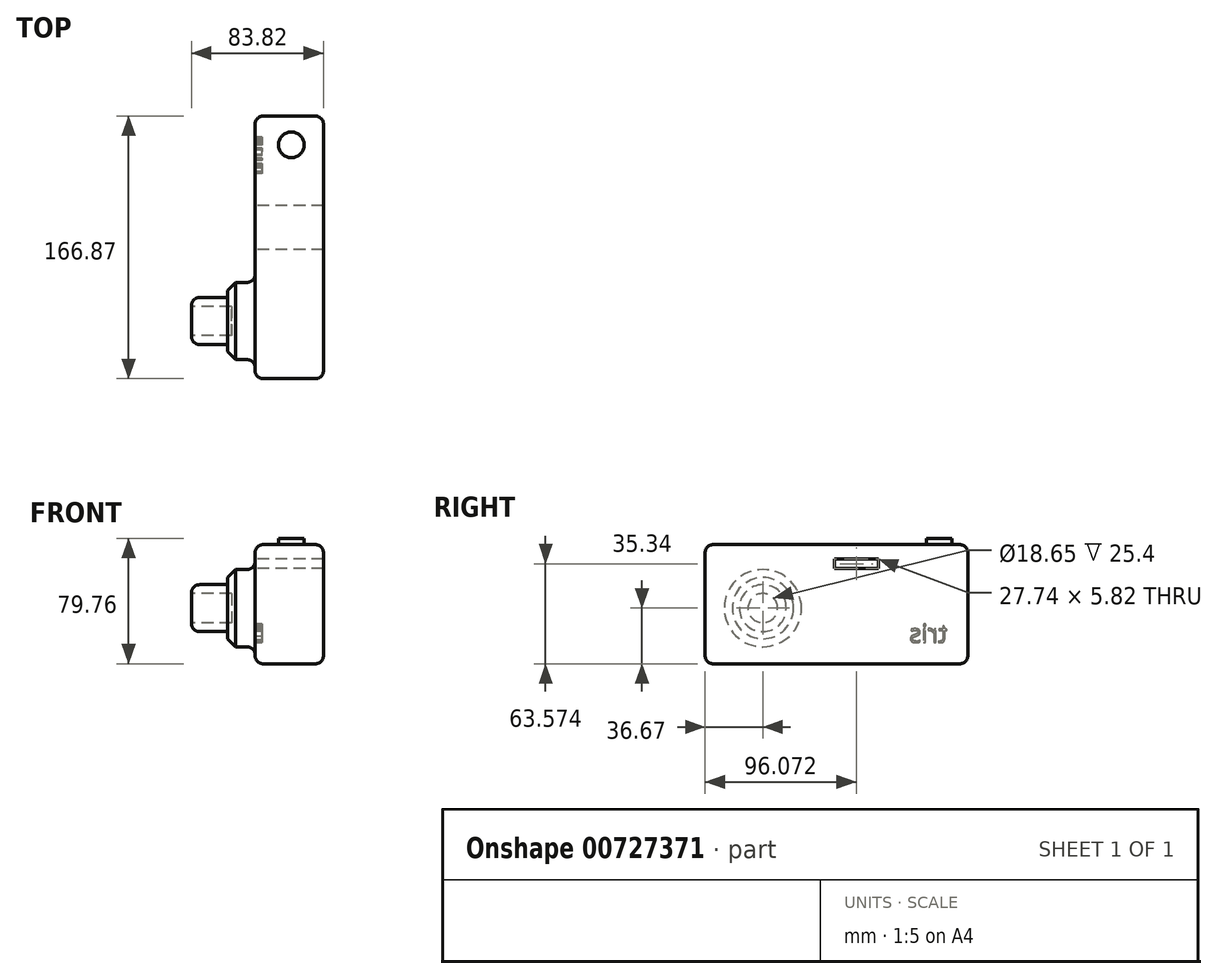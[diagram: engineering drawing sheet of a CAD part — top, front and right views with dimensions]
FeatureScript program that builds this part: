
annotation { "Feature Type Name" : "Feature", "Feature Type Description" : "" }
export const myFeature = defineFeature(function(context is Context, id is Id, definition is map)
    precondition{}
    {
        {
            var Q0;
            Q0=qCreatedBy(makeId("Top.planeOp"),FACE);
            var sketch = newSketch(context, id + "F0", { "sketchPlane" : qUnion([Q0])});
            skLineSegment(sketch, "E0.bottom", {"start": v(-47.57, -71.21) * mm, "end": v(-91, -71.21) * mm});
            skLineSegment(sketch, "E0.top", {"start": v(-47.57, 95.66) * mm, "end": v(-91, 95.66) * mm});
            skLineSegment(sketch, "E0.left", {"start": v(-47.57, -71.21) * mm, "end": v(-47.57, 95.66) * mm});
            skLineSegment(sketch, "E0.right", {"start": v(-91, -71.21) * mm, "end": v(-91, 95.66) * mm});
            skSolve(sketch);
        }
        {
            var Q0;
            Q0 = qSketchRegion(id + "F0", true);
            extrude(context, id + "F1", {"entities" : qUnion([Q0]), "depth" : 75.7 * mm, "offsetDistance" : 25.4 * mm});
        }
        {
            var Q0;
            Q0=makeQuery(id+"F1.opExtrude","SWEPT_FACE",FACE,{"disambiguationData":[OSD([sQuery(id+"F0.wireOp",EDGE,"E0.right")])]});
            var sketch = newSketch(context, id + "F2", { "sketchPlane" : qUnion([Q0])});
            skCircle(sketch, "E1", {"center": v(34.54, 35.34) * mm, "radius": 24.52 * mm});
            skSolve(sketch);
        }
        {
            var Q0;
            Q0 = qSketchRegion(id + "F2", true);
            extrude(context, id + "F3", {"entities" : qUnion([Q0]), "operationType" : NewBodyOperationType.ADD, "depth" : 17.53 * mm, "offsetDistance" : 25.4 * mm});
        }
        {
            var Q0;
            Q0=makeQuery(id+"F3.opExtrude","CAP_FACE",FACE,{"disambiguationData":[OSD([sQuery(id+"F2.wireOp",EDGE,"E1")])],"isStart":false});
            var sketch = newSketch(context, id + "F4", { "sketchPlane" : qUnion([Q0])});
            skCircle(sketch, "E2", {"center": v(34.54, 35.34) * mm, "radius": 14.9 * mm});
            skSolve(sketch);
        }
        {
            var Q0;
            Q0=makeQuery(id+"F4.imprint","IMPRINT",FACE,{"disambiguationData":[TD([[makeQuery(id+"F4.imprint","IMPRINT",EDGE,{"derivedFrom":sQuery(id+"F4.wireOp",EDGE,"E2")}),1.0]])]});
            var sketch = newSketch(context, id + "F5", { "sketchPlane" : qUnion([Q0])});
            skSolve(sketch);
        }
        {
            var Q0;
            Q0 = qSketchRegion(id + "F5", true);
            var Q1;
            Q1=makeQuery(id+"F5.imprint","IMPRINT",FACE,{"disambiguationData":[TD([[makeQuery(id+"F5.imprint","IMPRINT",EDGE,{"derivedFrom":makeQuery(id+"F4.imprint","IMPRINT",EDGE,{"derivedFrom":sQuery(id+"F4.wireOp",EDGE,"E2")})}),1.0]])]});
            extrude(context, id + "F6", {"entities" : qUnion([Q0, Q1]), "operationType" : NewBodyOperationType.ADD, "depth" : 5.33 * mm, "offsetDistance" : 25.4 * mm});
        }
        {
            var Q0;
            Q0=makeQuery(id+"F1.opExtrude","SWEPT_FACE",FACE,{"disambiguationData":[OSD([sQuery(id+"F0.wireOp",EDGE,"E0.right")])]});
            fillet(context, id + "F7", {"entities" : qUnion([Q0]), "radius" : 5.08 * mm, "tangentPropagation" : true, "allowEdgeOverflow" : false});
        }
        {
            var Q0;
            Q0=makeQuery(id+"F1.opExtrude","SWEPT_FACE",FACE,{"disambiguationData":[OSD([sQuery(id+"F0.wireOp",EDGE,"E0.bottom")])]});
            fillet(context, id + "F8", {"entities" : qUnion([Q0]), "radius" : 5.08 * mm, "tangentPropagation" : true, "allowEdgeOverflow" : false});
        }
        {
            var Q0;
            Q0=makeQuery(id+"F1.opExtrude","SWEPT_FACE",FACE,{"disambiguationData":[OSD([sQuery(id+"F0.wireOp",EDGE,"E0.left")])]});
            fillet(context, id + "F9", {"entities" : qUnion([Q0]), "radius" : 5.08 * mm, "tangentPropagation" : true, "allowEdgeOverflow" : false});
        }
        {
            var Q0;
            Q0=makeQuery(id+"F1.opExtrude","SWEPT_FACE",FACE,{"disambiguationData":[OSD([sQuery(id+"F0.wireOp",EDGE,"E0.top")])]});
            fillet(context, id + "F10", {"entities" : qUnion([Q0]), "radius" : 5.08 * mm, "tangentPropagation" : true, "allowEdgeOverflow" : false});
        }
        {
            var Q0;
            Q0=makeQuery(id+"F1.opExtrude","SWEPT_FACE",FACE,{"disambiguationData":[OSD([sQuery(id+"F0.wireOp",EDGE,"E0.right")])]});
            var sketch = newSketch(context, id + "F11", { "sketchPlane" : qUnion([Q0])});
            skText(sketch, "E3", { "text": "tris", "fontName": "OpenSans-Regular.ttf"});
            const initialGuessF11  = {"E3": [-0.08247, 0.01358, 1, 0, 0.01158]};
            skSetInitialGuess(sketch, initialGuessF11);
            skSolve(sketch);
        }
        {
            var Q0;
            Q0 = qSketchRegion(id + "F11", true);
            extrude(context, id + "F12", {"entities" : qUnion([Q0]), "operationType" : NewBodyOperationType.REMOVE, "oppositeDirection" : true, "depth" : 4.6 * mm, "offsetDistance" : 25.4 * mm});
        }
        {
            var Q1;
            Q1=sQuery(id+"F4.wireOp",VERTEX,"E2.center");
            var Q2;
            Q2=makeQuery(id+"F6.opExtrude","CAP_FACE",FACE,{"disambiguationData":[OSD([sQuery(id+"F4.wireOp",EDGE,"E2")])],"isStart":false});
            loft(context, id + "F13", {"operationType" : NewBodyOperationType.ADD, "sheetProfilesArray" : [{ "sheetProfileEntities" : qUnion([Q1]) }, { "sheetProfileEntities" : qUnion([Q2]) }]});
        }
        {
            var Q0;
            Q0=makeQuery(id+"F6.opExtrude","CAP_FACE",FACE,{"disambiguationData":[OSD([sQuery(id+"F4.wireOp",EDGE,"E2")])],"isStart":false});
            extrude(context, id + "F14", {"entities" : qUnion([Q0]), "operationType" : NewBodyOperationType.ADD, "depth" : 17.53 * mm, "offsetDistance" : 25.4 * mm});
        }
        {
            var Q0;
            Q0=makeQuery(id+"F14.opExtrude","CAP_FACE",FACE,{"disambiguationData":[OSD([sQuery(id+"F4.wireOp",EDGE,"E2")])],"isStart":false});
            extrude(context, id + "F15", {"entities" : qUnion([Q0]), "operationType" : NewBodyOperationType.ADD, "oppositeDirection" : true, "depth" : 64 * mm, "offsetDistance" : 25.4 * mm});
        }
        {
            var Q0;
            Q0=makeQuery(id+"F14.opExtrude","CAP_FACE",FACE,{"disambiguationData":[OSD([sQuery(id+"F4.wireOp",EDGE,"E2")])],"isStart":false});
            extrude(context, id + "F16", {"entities" : qUnion([Q0]), "operationType" : NewBodyOperationType.ADD, "oppositeDirection" : true, "depth" : 13.2 * mm, "offsetDistance" : 25.4 * mm});
        }
        {
            var Q0;
            Q0=makeQuery(id+"F14.opExtrude","CAP_FACE",FACE,{"disambiguationData":[OSD([sQuery(id+"F4.wireOp",EDGE,"E2")])],"isStart":false});
            extrude(context, id + "F17", {"entities" : qUnion([Q0]), "operationType" : NewBodyOperationType.ADD, "oppositeDirection" : true, "depth" : 25.4 * mm, "offsetDistance" : 25.4 * mm});
        }
        {
            var Q0;
            Q0=makeQuery(id+"F14.opExtrude","CAP_FACE",FACE,{"disambiguationData":[OSD([sQuery(id+"F4.wireOp",EDGE,"E2")])],"isStart":false});
            var sketch = newSketch(context, id + "F18", { "sketchPlane" : qUnion([Q0])});
            skCircle(sketch, "E4", {"center": v(34.54, 35.34) * mm, "radius": 9.33 * mm});
            skSolve(sketch);
        }
        {
            var Q0;
            Q0 = qSketchRegion(id + "F18", true);
            extrude(context, id + "F19", {"entities" : qUnion([Q0]), "operationType" : NewBodyOperationType.REMOVE, "oppositeDirection" : true, "depth" : 25.4 * mm, "offsetDistance" : 25.4 * mm});
        }
        {
            var Q0;
            Q0=makeQuery(id+"F14.opExtrude","CAP_EDGE",EDGE,{"disambiguationData":[OSD([sQuery(id+"F4.wireOp",EDGE,"E2")])],"isStart":false});
            fillet(context, id + "F20", {"entities" : qUnion([Q0]), "radius" : 5.08 * mm, "tangentPropagation" : true, "allowEdgeOverflow" : false});
        }
        {
            var Q0;
            Q0=makeQuery(id+"F3.opExtrude","CAP_EDGE",EDGE,{"disambiguationData":[OSD([sQuery(id+"F2.wireOp",EDGE,"E1")])],"isStart":false});
            chamfer(context, id + "F21", {"entities" : qUnion([Q0]), "width" : 5.08 * mm, "tangentPropagation" : true});
        }
        {
            var Q0;
            Q0=makeQuery(id+"F1.opExtrude","CAP_FACE",FACE,{"disambiguationData":[OSD([sQuery(id+"F0.wireOp",EDGE,"E0.bottom"),sQuery(id+"F0.wireOp",EDGE,"E0.top"),sQuery(id+"F0.wireOp",EDGE,"E0.left"),sQuery(id+"F0.wireOp",EDGE,"E0.right")])],"isStart":false});
            var sketch = newSketch(context, id + "F22", { "sketchPlane" : qUnion([Q0])});
            skCircle(sketch, "E5", {"center": v(-67.98, 77.34) * mm, "radius": 8.12 * mm});
            skSolve(sketch);
        }
        {
            var Q0;
            Q0 = qSketchRegion(id + "F22", true);
            extrude(context, id + "F23", {"entities" : qUnion([Q0]), "operationType" : NewBodyOperationType.ADD, "depth" : 4.06 * mm, "offsetDistance" : 25.4 * mm});
        }
        {
            var Q0;
            Q0=makeQuery(id+"F1.opExtrude","SWEPT_FACE",FACE,{"disambiguationData":[OSD([sQuery(id+"F0.wireOp",EDGE,"E0.right")])]});
            var sketch = newSketch(context, id + "F24", { "sketchPlane" : qUnion([Q0])});
            skLineSegment(sketch, "E6.bottom", {"start": v(-38.73, 66.48) * mm, "end": v(-10.99, 66.48) * mm});
            skLineSegment(sketch, "E6.top", {"start": v(-38.73, 60.66) * mm, "end": v(-10.99, 60.66) * mm});
            skLineSegment(sketch, "E6.left", {"start": v(-38.73, 66.48) * mm, "end": v(-38.73, 60.66) * mm});
            skLineSegment(sketch, "E6.right", {"start": v(-10.99, 66.48) * mm, "end": v(-10.99, 60.66) * mm});
            skSolve(sketch);
        }
        {
            var Q0;
            Q0 = qSketchRegion(id + "F24", true);
            extrude(context, id + "F25", {"entities" : qUnion([Q0]), "operationType" : NewBodyOperationType.REMOVE, "oppositeDirection" : true, "depth" : 324.1 * mm, "offsetDistance" : 25.4 * mm});
        }
    });
